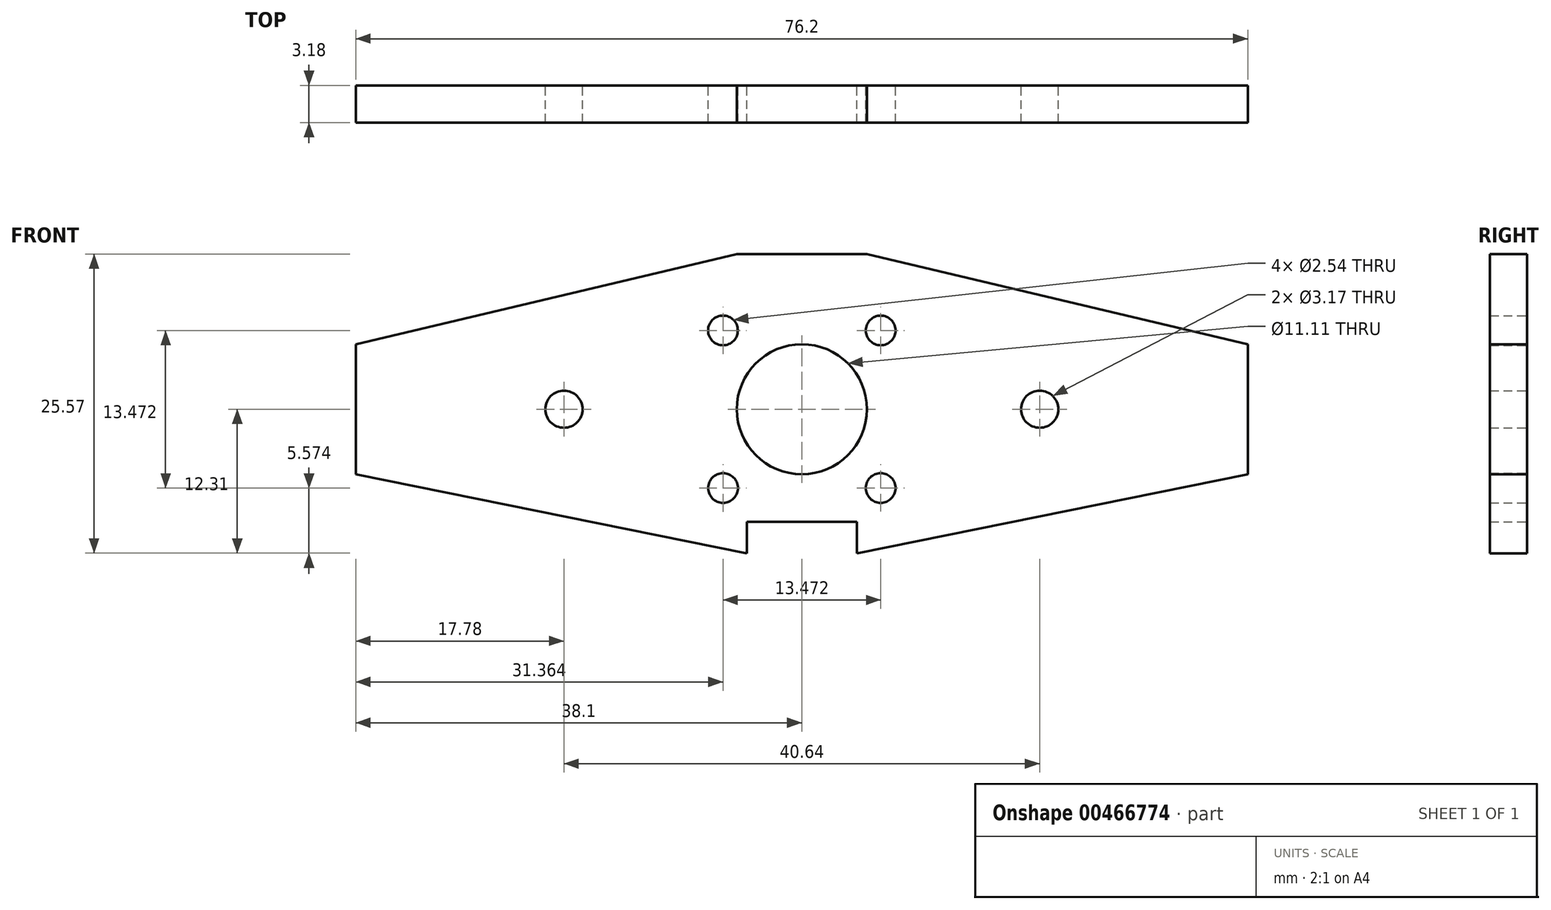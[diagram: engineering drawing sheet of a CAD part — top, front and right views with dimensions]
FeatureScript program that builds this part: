
annotation { "Feature Type Name" : "Feature", "Feature Type Description" : "" }
export const myFeature = defineFeature(function(context is Context, id is Id, definition is map)
    precondition{}
    {
        {
            var Q0;
            Q0=qCreatedBy(makeId("Front.planeOp"),FACE);
            var sketch = newSketch(context, id + "F0", { "sketchPlane" : qUnion([Q0])});
            skLineSegment(sketch, "E0.left", {"start": v(38.1, -5.56) * mm, "end": v(38.1, 5.56) * mm});
            skLineSegment(sketch, "E0.right", {"start": v(-38.1, -5.56) * mm, "end": v(-38.1, 5.56) * mm});
            skPoint(sketch, "E0.middle", {"position": v(0, 0) * mm});
            skLineSegment(sketch, "E1", {"start": v(-38.1, 5.56) * mm, "end": v(-5.56, 13.26) * mm});
            skLineSegment(sketch, "E2", {"start": v(-38.1, -5.56) * mm, "end": v(-4.7, -12.31) * mm});
            skLineSegment(sketch, "E3", {"start": v(38.1, 5.56) * mm, "end": v(5.56, 13.26) * mm});
            skLineSegment(sketch, "E4", {"start": v(38.1, -5.56) * mm, "end": v(4.7, -12.31) * mm});
            skCircle(sketch, "E5", {"center": v(0, 0) * mm, "radius": 5.56 * mm});
            skLineSegment(sketch, "E6.top", {"start": v(4.7, -9.62) * mm, "end": v(-4.7, -9.62) * mm});
            skLineSegment(sketch, "E6.left", {"start": v(4.7, -12.31) * mm, "end": v(4.7, -9.62) * mm});
            skLineSegment(sketch, "E6.right", {"start": v(-4.7, -12.31) * mm, "end": v(-4.7, -9.62) * mm});
            skLineSegment(sketch, "E7.bottom", {"start": v(-5.56, 13.26) * mm, "end": v(5.56, 13.26) * mm});
            skCircle(sketch, "E8", {"center": v(6.73, -6.73) * mm, "radius": 1.27 * mm});
            skCircle(sketch, "E9", {"center": v(-6.73, -6.74) * mm, "radius": 1.27 * mm});
            skCircle(sketch, "E10", {"center": v(-6.74, 6.74) * mm, "radius": 1.27 * mm});
            skCircle(sketch, "E11", {"center": v(6.74, 6.73) * mm, "radius": 1.27 * mm});
            skCircle(sketch, "E12", {"center": v(-20.32, 0) * mm, "radius": 1.59 * mm});
            skCircle(sketch, "E13", {"center": v(20.32, 0) * mm, "radius": 1.59 * mm});
            skSolve(sketch);
        }
        {
            var Q0;
            Q0=makeQuery(id+"F0.imprint","IMPRINT",FACE,{"disambiguationData":[TD([[makeQuery(id+"F0.imprint","IMPRINT",EDGE,{"derivedFrom":sQuery(id+"F0.wireOp",EDGE,"E0.left")}),1.0]])]});
            extrude(context, id + "F1", {"entities" : qUnion([Q0]), "depth" : 3.17 * mm});
        }
    });
